# Revit family: KEUCO_14977010000
name_source: partatom
category: Allgemeines Modell
revit_build: Autodesk Revit 2016 (Build: 20150220_1215(x64)
units: mm (PartAtom-declared; Revit-internal decimal feet)

## family parameters
Arbeitsebenenbasiert = Ja
Beim Laden mit Abzugskörper schneiden = Nein
Bemaßung runder Anschluss = Durchmesser verwenden
Gemeinsam genutzt = Nein
Immer vertikal = Nein
Kann Basisbauteil für Bewehrung sein = Nein
Raumberechnungspunkt = Nein
Teiletyp = Normal

## types (3) — shared parameters
Beschreibung = wandhängend
Fassungsvermögen: 3 l
Gewicht = 2.718
Hersteller = KEUCO
Kategorie = ACC
Material Hairtrockner = Schwarzgrau (RAL 7021)
Rail Length = 851 mm  [stored 2.79199 ft]
Serie = Plan
URL = https://www.keuco.com
Verwendung = WC / WP
Vorgabe-Ansicht = 1219 mm

## per-type parameters (varying)
| type | Ausschreibungstext | Stange Material |
| 14977070000 | KEUCO PLAN Hygieneabfallsammler 14977070000
Hygieneabfallsammler aus hochwertigem Edelstahl, 
zur Wandmontage, mit Deckel und Tretpedal
komplett mit herausnehmbarem Kunststoff-Einsatz 
für leichtes Reinigen, 3l Fassungsvermögen
Höhe 258 mm, Durchmesser 167 mm, Ausladung 240 mm
Der Hygieneabfallsammler wird verdeckt angebracht
Lieferung inkl. korrosionsfreiem Befestigungsmaterial | Edelstahl |
| 14977010000 | KEUCO PLAN Hygieneabfallsammler 14977010000
Hygieneabfallsammler in Chrom-finish (Edelstahl poliert), 
zur Wandmontage, mit Deckel und Tretpedal
komplett mit herausnehmbarem Kunststoff-Einsatz 
für leichtes Reinigen, 3l Fassungsvermögen
Höhe 258 mm, Durchmesser 167 mm, Ausladung 240 mm
Der Hygieneabfallsammler wird verdeckt angebracht
Lieferung inkl. korrosionsfreiem Befestigungsmaterial | Verchromt |
| 14977170000 | KEUCO PLAN Hygieneabfallsammler 14977170000
Hygieneabfallsammler in Aluminium silber-eloxiert (E6 EV1), 
zur Wandmontage, mit Deckel und Tretpedal
komplett mit herausnehmbarem Kunststoff-Einsatz 
für leichtes Reinigen, 3l Fassungsvermögen
Höhe 258 mm, Durchmesser 167 mm, Ausladung 240 mm
Der Hygieneabfallsammler wird verdeckt angebracht
Lieferung inkl. korrosionsfreiem Befestigungsmaterial | Verchromt |

note: column(s) folded — value = type name in every type: Artikelnummer

note: [stored X ft] marks values corroborated as IEEE doubles in the binary element streams (Revit-internal decimal feet)

## geometry (parser evidence)
native form markers: Sweep x3
no freeform markers — native parametric forms only
